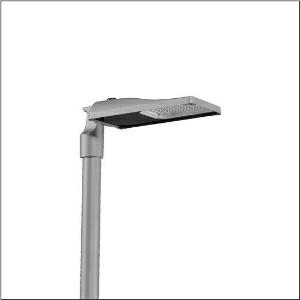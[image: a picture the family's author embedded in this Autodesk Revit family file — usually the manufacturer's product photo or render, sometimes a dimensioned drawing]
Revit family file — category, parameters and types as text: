
# Revit family: streetlight_sl_31_mini___st1_0a_5xh2d31s08ga_e80a
name_source: partatom
category: Lighting Fixtures
units: mm (PartAtom-declared; Revit-internal decimal feet)

## family parameters
Cut with Voids When Loaded = No
Host = Face
Light Source = No
Part Type = Normal
Room Calculation Point = No
Round Connector Dimension = Use Diameter
Shared = No

## types (1)
- --- (1 x LED, 5880 lm, 39.3 W, 3000K)
    Apparent Load = 39 VA
    CIE Flux Codes = 37 72 97 100 100
    Color Rendering = 70
    Color Temperature = 3000K
    Default Elevation = 1800 mm
    Description = Streetlight SL 31 mini D4i, Desk-Remote mast luminaire for post-top, side-entry; light control with lens of PMMA; light distribution: ST1.0a, direct asymmetric distribution, for standard-compliant lighting for roads and squares; LED: luminous flux: 5.880lm, light colour: 730, colour temperature: 3000K; luminous efficacy: 149,6lm/W; control: pre-setting: logarithmic dimming characteristic, flexible luminous flux parameterisation, time-dependent luminous flux control, constant luminous flux control, power reduction, intelligent temperature release in ECG and LED module, overheat protection; luminaire housing, of diecast aluminium, SITECO metallic grey (DB 702S), corrosivity category C5 high according to DIN EN ISO 12944; cover of toughened safety glass, transparent, mast flange of diecast aluminium, SITECO metallic grey (DB 702S), spigot size: 76/60mm, mast flange included unmounted; with cable H07RN-F 2x 1.5mm², cable length: 6,5m, connection cable pre-assembled; mains connection: 220..240V, AC, 50/60Hz; power consumption (at start of service life): 39,3W / (at end of service life): 40,7W / (with reduced operation 50%): 18,1W; protection rating (complete): IP66; insulation class (complete): insulation class II (safety insulation); impact resistance: IK10; certification: CE, ENEC, ENEC+, VDE, UKCA, ZD4i; permissible operating ambient temperature for outdoor applications: -40..+50°C; packaging unit: 1 piece

Light Distribution: ST1.0a
    Height = 76 mm
    Lamp = 1 x LED
    Lamp Light Flux = 5880 lm
    Lamp Power = 39.3 W
    Lamp count = 1
    Length = 547 mm
    Luminous efficacy = 150 lm/W
    Manufacturer = Siteco
    ModVariant = No
    Model = 5XH2D31S08GA
    Number of Poles = 1
    OnlyDefault = Yes
    Power Factor = 1
    Product Name = Streetlight SL 31 mini | ST1.0a
    Product group = mast luminaire | pylon top
    ProductGroupID = 6100
    Protection Class = Protection class II
    Protection Degree = IP 66
    RLX_Detail_Level = 1
    RLX_Emergency_Light_Flux = 0 lm
    RLX_Emergency_Type = 0
    RLX_Emergency_Type_DB = No
    RlxData = <blob elided: 39749 chars, md5=2ca50c46>
    Socket = socket
    Standby Power = 0 W
    System Light Flux = 5880 lm
    System Power = 39 W
    Type Comments = factory setting: luminous flux: 100 % | dim-lin: 254 | 798 mA
    Type Image = l_1300330.jpg
    URL = http://relux.com
    VarID = @adj_061493
    Voltage = 0 V
    Weight = 0.00 kg
    Width = 265 mm

## geometry (parser evidence)
native form markers: Blend x4, Sweep x10
no freeform markers — native parametric forms only
